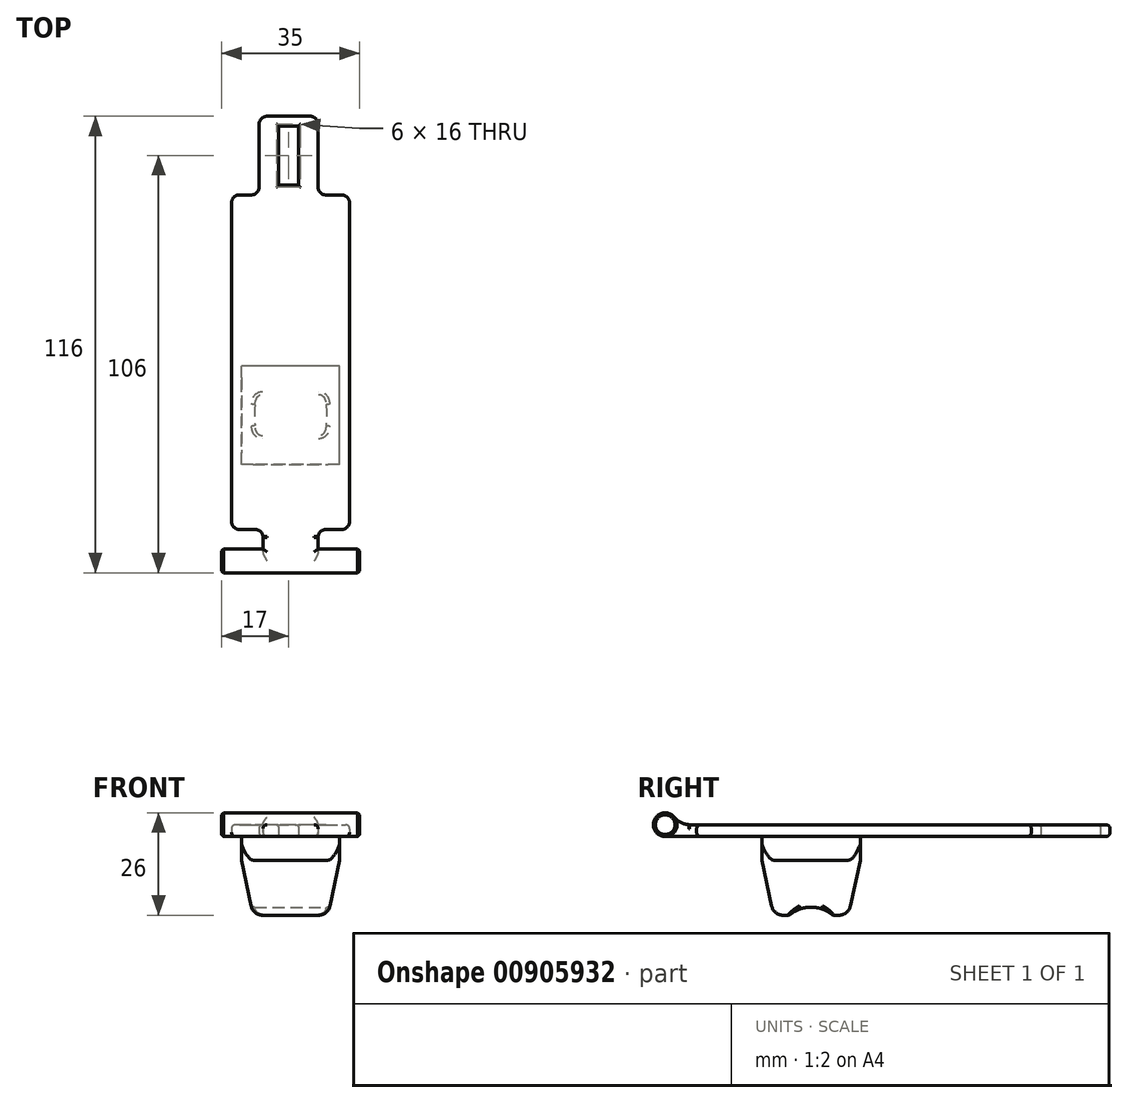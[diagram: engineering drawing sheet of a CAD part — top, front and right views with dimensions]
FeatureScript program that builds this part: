
annotation { "Feature Type Name" : "Feature", "Feature Type Description" : "" }
export const myFeature = defineFeature(function(context is Context, id is Id, definition is map)
    precondition{}
    {
        {
            var Q0;
            Q0=qCreatedBy(makeId("Top.planeOp"),FACE);
            var sketch = newSketch(context, id + "F0", { "sketchPlane" : qUnion([Q0])});
            skLineSegment(sketch, "E0", {"start": v(-7, 0) * mm, "end": v(7, 0) * mm});
            skLineSegment(sketch, "E1", {"start": v(7, 0) * mm, "end": v(7, 8) * mm});
            skLineSegment(sketch, "E2", {"start": v(7, 8) * mm, "end": v(15, 8) * mm});
            skLineSegment(sketch, "E3", {"start": v(15, 8) * mm, "end": v(15, 93) * mm});
            skLineSegment(sketch, "E4", {"start": v(15, 93) * mm, "end": v(7, 93) * mm});
            skLineSegment(sketch, "E5", {"start": v(7, 93) * mm, "end": v(7, 113) * mm});
            skLineSegment(sketch, "E6", {"start": v(7, 113) * mm, "end": v(-8, 113) * mm});
            skLineSegment(sketch, "E7", {"start": v(-8, 113) * mm, "end": v(-8, 93) * mm});
            skLineSegment(sketch, "E8", {"start": v(-8, 93) * mm, "end": v(-15, 93) * mm});
            skLineSegment(sketch, "E9", {"start": v(-15, 93) * mm, "end": v(-15, 8) * mm});
            skLineSegment(sketch, "E10", {"start": v(-15, 8) * mm, "end": v(-7, 8) * mm});
            skLineSegment(sketch, "E11", {"start": v(-7, 8) * mm, "end": v(-7, 0) * mm});
            skLineSegment(sketch, "E12", {"start": v(-0.5, 113) * mm, "end": v(-0.5, 93) * mm, "construction": true});
            skLineSegment(sketch, "E13", {"start": v(-8, 103) * mm, "end": v(7, 103) * mm, "construction": true});
            skLineSegment(sketch, "E14.bottom", {"start": v(-3, 110.5) * mm, "end": v(2, 110.5) * mm});
            skLineSegment(sketch, "E14.top", {"start": v(-3, 95.5) * mm, "end": v(2, 95.5) * mm});
            skLineSegment(sketch, "E14.left", {"start": v(-3, 110.5) * mm, "end": v(-3, 95.5) * mm});
            skLineSegment(sketch, "E14.right", {"start": v(2, 110.5) * mm, "end": v(2, 95.5) * mm});
            skPoint(sketch, "E14.middle", {"position": v(-0.5, 103) * mm});
            skSolve(sketch);
        }
        {
            var Q0;
            Q0 = qSketchRegion(id + "F0", true);
            extrude(context, id + "F1", {"entities" : qUnion([Q0]), "depth" : 3 * mm, "offsetDistance" : 25 * mm});
        }
        {
            var Q0;
            Q0=qCreatedBy(makeId("Right.planeOp"),FACE);
            var sketch = newSketch(context, id + "F2", { "sketchPlane" : qUnion([Q0])});
            skCircle(sketch, "E15", {"center": v(0, 3) * mm, "radius": 3 * mm});
            skSolve(sketch);
        }
        {
            var Q0;
            Q0 = qSketchRegion(id + "F2", true);
            extrude(context, id + "F3", {"entities" : qUnion([Q0]), "operationType" : NewBodyOperationType.ADD, "endBound" : BoundingType.SYMMETRIC, "depth" : 35 * mm, "offsetDistance" : 25 * mm});
        }
        {
            var Q0;
            Q0=makeQuery(id+"F1.opExtrude","SWEPT_EDGE",EDGE,{"disambiguationData":[OSD([sQuery(id+"F0.wireOp",EDGE,"E1"),sQuery(id+"F0.wireOp",EDGE,"E2")])]});
            var Q1;
            Q1=makeQuery(id+"F1.opExtrude","SWEPT_EDGE",EDGE,{"disambiguationData":[OSD([sQuery(id+"F0.wireOp",EDGE,"E10"),sQuery(id+"F0.wireOp",EDGE,"E11")])]});
            var Q2;
            Q2=makeQuery(id+"F1.opExtrude","SWEPT_EDGE",EDGE,{"disambiguationData":[OSD([sQuery(id+"F0.wireOp",EDGE,"E9"),sQuery(id+"F0.wireOp",EDGE,"E10")])]});
            var Q3;
            Q3=makeQuery(id+"F1.opExtrude","SWEPT_EDGE",EDGE,{"disambiguationData":[OSD([sQuery(id+"F0.wireOp",EDGE,"E2"),sQuery(id+"F0.wireOp",EDGE,"E3")])]});
            fillet(context, id + "F4", {"entities" : qUnion([Q0, Q1, Q2, Q3]), "radius" : 2 * mm, "tangentPropagation" : true, "allowEdgeOverflow" : false});
        }
        {
            var Q0;
            Q0=makeQuery(id+"F3.boolean.opBoolean","INTERSECT",EDGE,{"derivedFrom":[makeQuery(id+"F1.opExtrude","CAP_FACE",FACE,{"disambiguationData":[OSD([sQuery(id+"F0.wireOp",EDGE,"E0"),sQuery(id+"F0.wireOp",EDGE,"E1"),sQuery(id+"F0.wireOp",EDGE,"E2"),sQuery(id+"F0.wireOp",EDGE,"E3"),sQuery(id+"F0.wireOp",EDGE,"E4"),sQuery(id+"F0.wireOp",EDGE,"E5"),sQuery(id+"F0.wireOp",EDGE,"E6"),sQuery(id+"F0.wireOp",EDGE,"E7"),sQuery(id+"F0.wireOp",EDGE,"E8"),sQuery(id+"F0.wireOp",EDGE,"E9"),sQuery(id+"F0.wireOp",EDGE,"E10"),sQuery(id+"F0.wireOp",EDGE,"E11"),sQuery(id+"F0.wireOp",EDGE,"E14.bottom"),sQuery(id+"F0.wireOp",EDGE,"E14.top"),sQuery(id+"F0.wireOp",EDGE,"E14.left"),sQuery(id+"F0.wireOp",EDGE,"E14.right")])],"isStart":false}),makeQuery(id+"F3.opExtrude","SWEPT_FACE",FACE,{"disambiguationData":[OSD([sQuery(id+"F2.wireOp",EDGE,"E15")])]})]});
            fillet(context, id + "F5", {"entities" : qUnion([Q0]), "radius" : 5 * mm, "tangentPropagation" : true, "allowEdgeOverflow" : false});
        }
        {
            var Q0;
            Q0=makeQuery(id+"F1.opExtrude","SWEPT_EDGE",EDGE,{"disambiguationData":[OSD([sQuery(id+"F0.wireOp",EDGE,"E3"),sQuery(id+"F0.wireOp",EDGE,"E4")])]});
            var Q1;
            Q1=makeQuery(id+"F1.opExtrude","SWEPT_EDGE",EDGE,{"disambiguationData":[OSD([sQuery(id+"F0.wireOp",EDGE,"E4"),sQuery(id+"F0.wireOp",EDGE,"E5")])]});
            var Q2;
            Q2=makeQuery(id+"F1.opExtrude","SWEPT_EDGE",EDGE,{"disambiguationData":[OSD([sQuery(id+"F0.wireOp",EDGE,"E8"),sQuery(id+"F0.wireOp",EDGE,"E9")])]});
            var Q3;
            Q3=makeQuery(id+"F1.opExtrude","SWEPT_EDGE",EDGE,{"disambiguationData":[OSD([sQuery(id+"F0.wireOp",EDGE,"E7"),sQuery(id+"F0.wireOp",EDGE,"E8")])]});
            var Q4;
            Q4=makeQuery(id+"F1.opExtrude","SWEPT_EDGE",EDGE,{"disambiguationData":[OSD([sQuery(id+"F0.wireOp",EDGE,"E6"),sQuery(id+"F0.wireOp",EDGE,"E7")])]});
            var Q5;
            Q5=makeQuery(id+"F1.opExtrude","SWEPT_EDGE",EDGE,{"disambiguationData":[OSD([sQuery(id+"F0.wireOp",EDGE,"E5"),sQuery(id+"F0.wireOp",EDGE,"E6")])]});
            fillet(context, id + "F6", {"entities" : qUnion([Q0, Q1, Q2, Q3, Q4, Q5]), "radius" : 2 * mm, "tangentPropagation" : true, "allowEdgeOverflow" : false});
        }
        {
            var Q0;
            Q0=makeQuery(id+"F1.opExtrude","CAP_EDGE",EDGE,{"disambiguationData":[OSD([sQuery(id+"F0.wireOp",EDGE,"E9")])],"isStart":false});
            var Q1;
            Q1=makeQuery(id+"F1.opExtrude","CAP_EDGE",EDGE,{"disambiguationData":[OSD([sQuery(id+"F0.wireOp",EDGE,"E9")])],"isStart":true});
            fillet(context, id + "F7", {"entities" : qUnion([Q0, Q1]), "radius" : 1 * mm, "tangentPropagation" : true, "allowEdgeOverflow" : false});
        }
        {
            var Q0;
            Q0=makeQuery(id+"F1.opExtrude","CAP_EDGE",EDGE,{"disambiguationData":[OSD([sQuery(id+"F0.wireOp",EDGE,"E14.top")])],"isStart":false});
            var Q1;
            Q1=makeQuery(id+"F1.opExtrude","CAP_EDGE",EDGE,{"disambiguationData":[OSD([sQuery(id+"F0.wireOp",EDGE,"E14.left")])],"isStart":false});
            var Q2;
            Q2=makeQuery(id+"F1.opExtrude","CAP_EDGE",EDGE,{"disambiguationData":[OSD([sQuery(id+"F0.wireOp",EDGE,"E14.right")])],"isStart":false});
            var Q3;
            Q3=makeQuery(id+"F1.opExtrude","CAP_EDGE",EDGE,{"disambiguationData":[OSD([sQuery(id+"F0.wireOp",EDGE,"E14.bottom")])],"isStart":false});
            var Q4;
            Q4=makeQuery(id+"F1.opExtrude","CAP_EDGE",EDGE,{"disambiguationData":[OSD([sQuery(id+"F0.wireOp",EDGE,"E14.left")])],"isStart":true});
            var Q5;
            Q5=makeQuery(id+"F1.opExtrude","CAP_EDGE",EDGE,{"disambiguationData":[OSD([sQuery(id+"F0.wireOp",EDGE,"E14.top")])],"isStart":true});
            var Q6;
            Q6=makeQuery(id+"F1.opExtrude","CAP_EDGE",EDGE,{"disambiguationData":[OSD([sQuery(id+"F0.wireOp",EDGE,"E14.bottom")])],"isStart":true});
            var Q7;
            Q7=makeQuery(id+"F1.opExtrude","CAP_EDGE",EDGE,{"disambiguationData":[OSD([sQuery(id+"F0.wireOp",EDGE,"E14.right")])],"isStart":true});
            fillet(context, id + "F8", {"entities" : qUnion([Q0, Q1, Q2, Q3, Q4, Q5, Q6, Q7]), "radius" : .5 * mm, "tangentPropagation" : true, "allowEdgeOverflow" : false});
        }
        {
            var Q0;
            Q0=makeQuery(id+"F3.opExtrude","CAP_EDGE",EDGE,{"disambiguationData":[OSD([sQuery(id+"F2.wireOp",EDGE,"E15")])],"isStart":false});
            var Q1;
            Q1=makeQuery(id+"F3.opExtrude","CAP_EDGE",EDGE,{"disambiguationData":[OSD([sQuery(id+"F2.wireOp",EDGE,"E15")])],"isStart":true});
            chamfer(context, id + "F9", {"entities" : qUnion([Q0, Q1]), "width" : .5 * mm, "tangentPropagation" : true});
        }
        {
            var Q0;
            Q0=makeQuery(id+"F1.opExtrude","CAP_FACE",FACE,{"disambiguationData":[OSD([sQuery(id+"F0.wireOp",EDGE,"E0"),sQuery(id+"F0.wireOp",EDGE,"E1"),sQuery(id+"F0.wireOp",EDGE,"E2"),sQuery(id+"F0.wireOp",EDGE,"E3"),sQuery(id+"F0.wireOp",EDGE,"E4"),sQuery(id+"F0.wireOp",EDGE,"E5"),sQuery(id+"F0.wireOp",EDGE,"E6"),sQuery(id+"F0.wireOp",EDGE,"E7"),sQuery(id+"F0.wireOp",EDGE,"E8"),sQuery(id+"F0.wireOp",EDGE,"E9"),sQuery(id+"F0.wireOp",EDGE,"E10"),sQuery(id+"F0.wireOp",EDGE,"E11"),sQuery(id+"F0.wireOp",EDGE,"E14.bottom"),sQuery(id+"F0.wireOp",EDGE,"E14.top"),sQuery(id+"F0.wireOp",EDGE,"E14.left"),sQuery(id+"F0.wireOp",EDGE,"E14.right")])],"isStart":true});
            var sketch = newSketch(context, id + "F10", { "sketchPlane" : qUnion([Q0])});
            skLineSegment(sketch, "E16.bottom", {"start": v(12.5, -24.55) * mm, "end": v(-12.5, -24.55) * mm});
            skLineSegment(sketch, "E16.top", {"start": v(12.5, -49.55) * mm, "end": v(-12.5, -49.55) * mm});
            skLineSegment(sketch, "E16.left", {"start": v(12.5, -24.55) * mm, "end": v(12.5, -49.55) * mm});
            skLineSegment(sketch, "E16.right", {"start": v(-12.5, -24.55) * mm, "end": v(-12.5, -49.55) * mm});
            skPoint(sketch, "E16.middle", {"position": v(0, -37.05) * mm});
            skSolve(sketch);
        }
        {
            var Q0;
            Q0 = qSketchRegion(id + "F10", true);
            extrude(context, id + "F11", {"entities" : qUnion([Q0]), "operationType" : NewBodyOperationType.ADD, "depth" : 20 * mm, "offsetDistance" : 25 * mm});
        }
        {
            var Q0;
            Q0=makeQuery(id+"F11.opExtrude","CAP_EDGE",EDGE,{"disambiguationData":[OSD([sQuery(id+"F10.wireOp",EDGE,"E16.bottom")])],"isStart":false});
            var Q1;
            Q1=makeQuery(id+"F11.opExtrude","CAP_EDGE",EDGE,{"disambiguationData":[OSD([sQuery(id+"F10.wireOp",EDGE,"E16.left")])],"isStart":false});
            var Q2;
            Q2=makeQuery(id+"F11.opExtrude","CAP_EDGE",EDGE,{"disambiguationData":[OSD([sQuery(id+"F10.wireOp",EDGE,"E16.top")])],"isStart":false});
            var Q3;
            Q3=makeQuery(id+"F11.opExtrude","CAP_EDGE",EDGE,{"disambiguationData":[OSD([sQuery(id+"F10.wireOp",EDGE,"E16.right")])],"isStart":false});
            chamfer(context, id + "F12", {"entities" : qUnion([Q0, Q1, Q2, Q3]), "chamferType" : ChamferType.TWO_OFFSETS, "width1" : 3 * mm, "oppositeDirection" : false, "width2" : 14 * mm, "tangentPropagation" : true});
        }
        {
            var Q0;
            {var subQ0=sQuery(id+"F10.wireOp",EDGE,"E16.left");Q0=makeQuery(id+"F12.opChamfer","BLEND_EDGE",EDGE,{"blendedFrom":[makeQuery(id+"F11.opExtrude","CAP_EDGE",EDGE,{"disambiguationData":[OSD([subQ0])],"isStart":false}),makeQuery(id+"F11.opExtrude","CAP_FACE",FACE,{"disambiguationData":[OSD([sQuery(id+"F10.wireOp",EDGE,"E16.bottom"),sQuery(id+"F10.wireOp",EDGE,"E16.top"),subQ0,sQuery(id+"F10.wireOp",EDGE,"E16.right")])],"isStart":false})],"blendedInto":[makeQuery(id+"F11.opExtrude","CAP_FACE",FACE,{"disambiguationData":[OSD([sQuery(id+"F10.wireOp",EDGE,"E16.bottom"),sQuery(id+"F10.wireOp",EDGE,"E16.top"),subQ0,sQuery(id+"F10.wireOp",EDGE,"E16.right")])],"isStart":false})]});}
            var Q1;
            {var subQ0=sQuery(id+"F10.wireOp",EDGE,"E16.bottom");Q1=makeQuery(id+"F12.opChamfer","BLEND_EDGE",EDGE,{"blendedFrom":[makeQuery(id+"F11.opExtrude","CAP_EDGE",EDGE,{"disambiguationData":[OSD([subQ0])],"isStart":false}),makeQuery(id+"F11.opExtrude","CAP_FACE",FACE,{"disambiguationData":[OSD([subQ0,sQuery(id+"F10.wireOp",EDGE,"E16.top"),sQuery(id+"F10.wireOp",EDGE,"E16.left"),sQuery(id+"F10.wireOp",EDGE,"E16.right")])],"isStart":false})],"blendedInto":[makeQuery(id+"F11.opExtrude","CAP_FACE",FACE,{"disambiguationData":[OSD([subQ0,sQuery(id+"F10.wireOp",EDGE,"E16.top"),sQuery(id+"F10.wireOp",EDGE,"E16.left"),sQuery(id+"F10.wireOp",EDGE,"E16.right")])],"isStart":false})]});}
            var Q2;
            {var subQ0=sQuery(id+"F10.wireOp",EDGE,"E16.top");Q2=makeQuery(id+"F12.opChamfer","BLEND_EDGE",EDGE,{"blendedFrom":[makeQuery(id+"F11.opExtrude","CAP_EDGE",EDGE,{"disambiguationData":[OSD([subQ0])],"isStart":false}),makeQuery(id+"F11.opExtrude","CAP_FACE",FACE,{"disambiguationData":[OSD([sQuery(id+"F10.wireOp",EDGE,"E16.bottom"),subQ0,sQuery(id+"F10.wireOp",EDGE,"E16.left"),sQuery(id+"F10.wireOp",EDGE,"E16.right")])],"isStart":false})],"blendedInto":[makeQuery(id+"F11.opExtrude","CAP_FACE",FACE,{"disambiguationData":[OSD([sQuery(id+"F10.wireOp",EDGE,"E16.bottom"),subQ0,sQuery(id+"F10.wireOp",EDGE,"E16.left"),sQuery(id+"F10.wireOp",EDGE,"E16.right")])],"isStart":false})]});}
            var Q3;
            {var subQ0=sQuery(id+"F10.wireOp",EDGE,"E16.right");Q3=makeQuery(id+"F12.opChamfer","BLEND_EDGE",EDGE,{"blendedFrom":[makeQuery(id+"F11.opExtrude","CAP_EDGE",EDGE,{"disambiguationData":[OSD([subQ0])],"isStart":false}),makeQuery(id+"F11.opExtrude","CAP_FACE",FACE,{"disambiguationData":[OSD([sQuery(id+"F10.wireOp",EDGE,"E16.bottom"),sQuery(id+"F10.wireOp",EDGE,"E16.top"),sQuery(id+"F10.wireOp",EDGE,"E16.left"),subQ0])],"isStart":false})],"blendedInto":[makeQuery(id+"F11.opExtrude","CAP_FACE",FACE,{"disambiguationData":[OSD([sQuery(id+"F10.wireOp",EDGE,"E16.bottom"),sQuery(id+"F10.wireOp",EDGE,"E16.top"),sQuery(id+"F10.wireOp",EDGE,"E16.left"),subQ0])],"isStart":false})]});}
            var Q4;
            Q4=makeQuery(id+"F12.opChamfer","BLEND_EDGE",EDGE,{"blendedFrom":[makeQuery(id+"F11.opExtrude","CAP_EDGE",EDGE,{"disambiguationData":[OSD([sQuery(id+"F10.wireOp",EDGE,"E16.bottom")])],"isStart":false}),makeQuery(id+"F11.opExtrude","CAP_EDGE",EDGE,{"disambiguationData":[OSD([sQuery(id+"F10.wireOp",EDGE,"E16.right")])],"isStart":false})],"blendedInto":[]});
            var Q5;
            Q5=makeQuery(id+"F12.opChamfer","BLEND_EDGE",EDGE,{"blendedFrom":[makeQuery(id+"F11.opExtrude","CAP_EDGE",EDGE,{"disambiguationData":[OSD([sQuery(id+"F10.wireOp",EDGE,"E16.bottom")])],"isStart":false}),makeQuery(id+"F11.opExtrude","CAP_EDGE",EDGE,{"disambiguationData":[OSD([sQuery(id+"F10.wireOp",EDGE,"E16.left")])],"isStart":false})],"blendedInto":[]});
            var Q6;
            Q6=makeQuery(id+"F12.opChamfer","BLEND_EDGE",EDGE,{"blendedFrom":[makeQuery(id+"F11.opExtrude","CAP_EDGE",EDGE,{"disambiguationData":[OSD([sQuery(id+"F10.wireOp",EDGE,"E16.top")])],"isStart":false}),makeQuery(id+"F11.opExtrude","CAP_EDGE",EDGE,{"disambiguationData":[OSD([sQuery(id+"F10.wireOp",EDGE,"E16.right")])],"isStart":false})],"blendedInto":[]});
            var Q7;
            Q7=makeQuery(id+"F12.opChamfer","BLEND_EDGE",EDGE,{"blendedFrom":[makeQuery(id+"F11.opExtrude","CAP_EDGE",EDGE,{"disambiguationData":[OSD([sQuery(id+"F10.wireOp",EDGE,"E16.top")])],"isStart":false}),makeQuery(id+"F11.opExtrude","CAP_EDGE",EDGE,{"disambiguationData":[OSD([sQuery(id+"F10.wireOp",EDGE,"E16.left")])],"isStart":false})],"blendedInto":[]});
            fillet(context, id + "F13", {"entities" : qUnion([Q0, Q1, Q2, Q3, Q4, Q5, Q6, Q7]), "radius" : 3 * mm, "tangentPropagation" : true, "allowEdgeOverflow" : false});
        }
        {
            var Q0;
            Q0=qCreatedBy(makeId("Right.planeOp"),FACE);
            var sketch = newSketch(context, id + "F14", { "sketchPlane" : qUnion([Q0])});
            skCircle(sketch, "E17", {"center": v(37.05, -26.43) * mm, "radius": 8.48 * mm});
            skLineSegment(sketch, "E18", {"start": v(1, 0) * mm, "end": v(54.52, 0) * mm, "construction": true});
            skLineSegment(sketch, "E19", {"start": v(37.05, 0) * mm, "end": v(37.05, -37.14) * mm, "construction": true});
            skSolve(sketch);
        }
        {
            var Q0;
            Q0 = qSketchRegion(id + "F14", true);
            extrude(context, id + "F15", {"entities" : qUnion([Q0]), "operationType" : NewBodyOperationType.REMOVE, "endBound" : BoundingType.SYMMETRIC, "oppositeDirection" : true, "depth" : 25 * mm, "offsetDistance" : 25 * mm});
        }
        {
            var Q0;
            Q0=makeQuery(id+"F15.boolean.opBoolean","INTERSECT",EDGE,{"disambiguationData":[OD(0.0)],"derivedFrom":[makeQuery(id+"F11.opExtrude","CAP_FACE",FACE,{"disambiguationData":[OSD([sQuery(id+"F10.wireOp",EDGE,"E16.bottom"),sQuery(id+"F10.wireOp",EDGE,"E16.top"),sQuery(id+"F10.wireOp",EDGE,"E16.left"),sQuery(id+"F10.wireOp",EDGE,"E16.right")])],"isStart":false}),makeQuery(id+"F15.opExtrude","SWEPT_FACE",FACE,{"disambiguationData":[OSD([sQuery(id+"F14.wireOp",EDGE,"E17")])]})]});
            fillet(context, id + "F16", {"entities" : qUnion([Q0]), "radius" : 1 * mm, "tangentPropagation" : true, "allowEdgeOverflow" : false});
        }
    });
